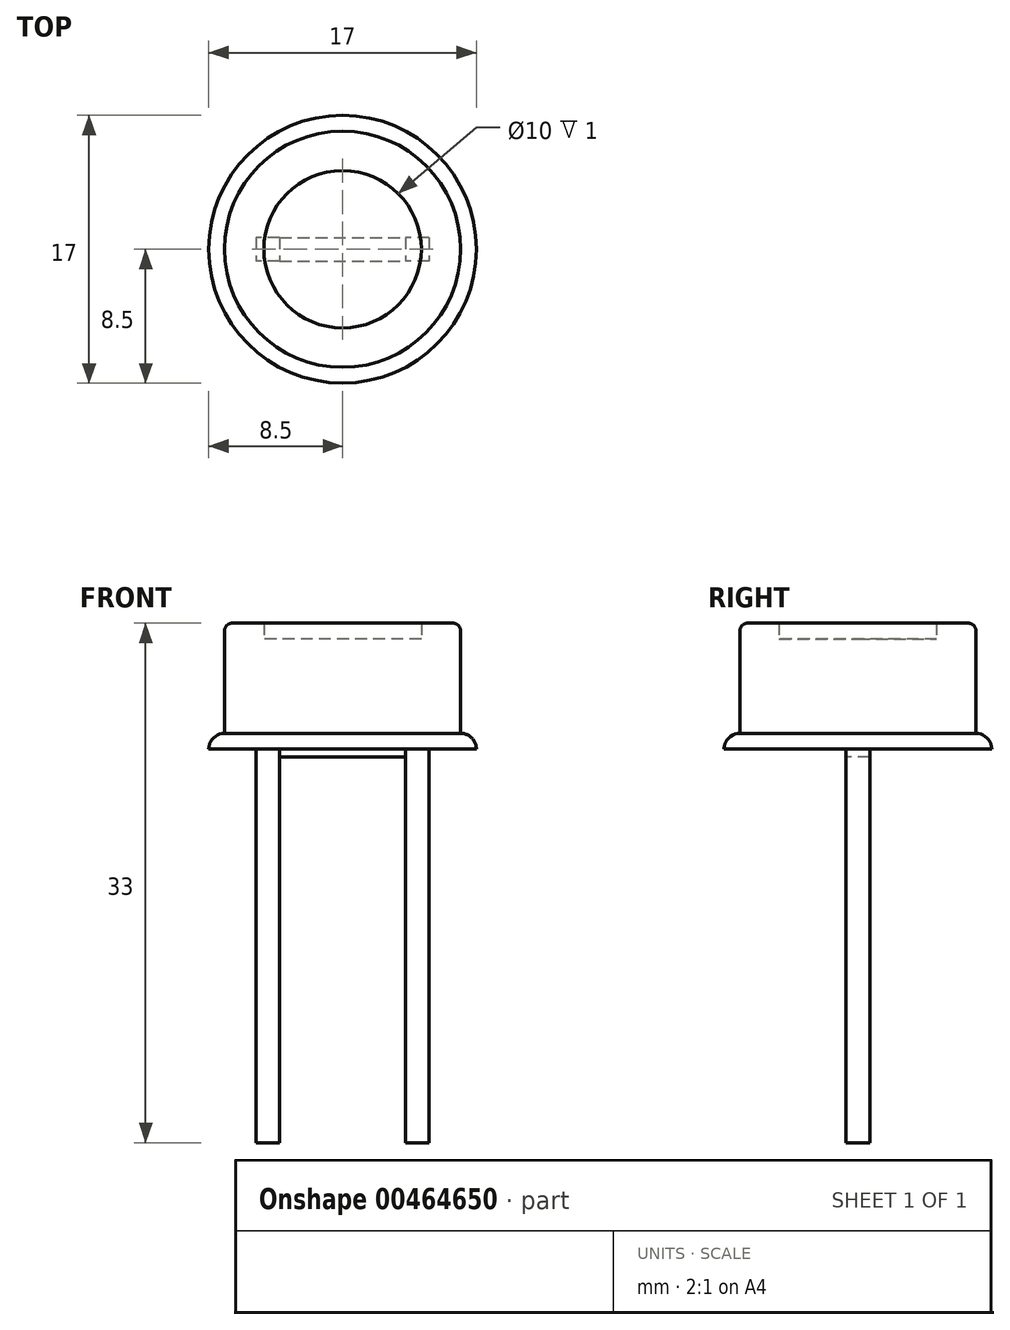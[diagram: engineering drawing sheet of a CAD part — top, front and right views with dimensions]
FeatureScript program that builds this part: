
annotation { "Feature Type Name" : "Feature", "Feature Type Description" : "" }
export const myFeature = defineFeature(function(context is Context, id is Id, definition is map)
    precondition{}
    {
        {
            var Q0;
            Q0=qCreatedBy(makeId("Top.planeOp"),FACE);
            var sketch = newSketch(context, id + "F0", { "sketchPlane" : qUnion([Q0])});
            skCircle(sketch, "E0", {"center": v(0, 0) * mm, "radius": 7.5 * mm});
            skCircle(sketch, "E1", {"center": v(0, 0) * mm, "radius": 5 * mm});
            skCircle(sketch, "E2", {"center": v(0, 0) * mm, "radius": 8.5 * mm});
            skSolve(sketch);
        }
        {
            var Q0;
            Q0=makeQuery(id+"F0.imprint","IMPRINT",FACE,{"disambiguationData":[TD([[makeQuery(id+"F0.imprint","IMPRINT",EDGE,{"derivedFrom":sQuery(id+"F0.wireOp",EDGE,"E1")}),1.0]])]});
            extrude(context, id + "F1", {"entities" : qUnion([Q0]), "depth" : 7 * mm});
        }
        {
            var Q0;
            Q0=makeQuery(id+"F0.imprint","IMPRINT",FACE,{"disambiguationData":[TD([[makeQuery(id+"F0.imprint","IMPRINT",EDGE,{"derivedFrom":sQuery(id+"F0.wireOp",EDGE,"E0")}),1.0]])]});
            extrude(context, id + "F2", {"entities" : qUnion([Q0]), "operationType" : NewBodyOperationType.ADD, "depth" : 8 * mm});
        }
        {
            var Q0;
            Q0=makeQuery(id+"F0.imprint","IMPRINT",FACE,{"disambiguationData":[TD([[makeQuery(id+"F0.imprint","IMPRINT",EDGE,{"derivedFrom":sQuery(id+"F0.wireOp",EDGE,"E0")}),-1.0]])]});
            extrude(context, id + "F3", {"entities" : qUnion([Q0]), "operationType" : NewBodyOperationType.ADD, "depth" : 1 * mm});
        }
        {
            var Q0;
            Q0=makeQuery(id+"F3.opExtrude","CAP_EDGE",EDGE,{"disambiguationData":[OSD([sQuery(id+"F0.wireOp",EDGE,"E2")])],"isStart":false});
            fillet(context, id + "F4", {"entities" : qUnion([Q0]), "radius" : 1 * mm, "tangentPropagation" : true, "allowEdgeOverflow" : false});
        }
        {
            var Q0;
            Q0=makeQuery(id+"F2.opExtrude","CAP_EDGE",EDGE,{"disambiguationData":[OSD([sQuery(id+"F0.wireOp",EDGE,"E0")])],"isStart":false});
            fillet(context, id + "F5", {"entities" : qUnion([Q0]), "radius" : .5 * mm, "tangentPropagation" : true, "allowEdgeOverflow" : false});
        }
        {
            var Q0;
            {var subQ0=sQuery(id+"F0.wireOp",EDGE,"E0");var subQ1=sQuery(id+"F0.wireOp",EDGE,"E1");Q0=makeQuery(id+"F3.boolean.opBoolean","MERGE",FACE,{"derivedFrom":[makeQuery(id+"F2.boolean.opBoolean","MERGE",FACE,{"derivedFrom":[makeQuery(id+"F1.opExtrude","CAP_FACE",FACE,{"disambiguationData":[OSD([subQ1])],"isStart":true}),makeQuery(id+"F2.opExtrude","CAP_FACE",FACE,{"disambiguationData":[OSD([subQ0,subQ1])],"isStart":true})]}),makeQuery(id+"F3.opExtrude","CAP_FACE",FACE,{"disambiguationData":[OSD([subQ0,sQuery(id+"F0.wireOp",EDGE,"E2")])],"isStart":true})]});}
            var sketch = newSketch(context, id + "F6", { "sketchPlane" : qUnion([Q0])});
            skLineSegment(sketch, "E3.bottom", {"start": v(5.5, -0.75) * mm, "end": v(4, -0.75) * mm});
            skLineSegment(sketch, "E3.top", {"start": v(5.5, 0.75) * mm, "end": v(4, 0.75) * mm});
            skLineSegment(sketch, "E3.left", {"start": v(5.5, -0.75) * mm, "end": v(5.5, 0.75) * mm});
            skLineSegment(sketch, "E3.right", {"start": v(4, -0.75) * mm, "end": v(4, 0.75) * mm});
            skPoint(sketch, "E3.middle", {"position": v(4.75, 0) * mm});
            skLineSegment(sketch, "E4.bottom", {"start": v(-4, -0.75) * mm, "end": v(-5.5, -0.75) * mm});
            skLineSegment(sketch, "E4.top", {"start": v(-4, 0.75) * mm, "end": v(-5.5, 0.75) * mm});
            skLineSegment(sketch, "E4.left", {"start": v(-4, -0.75) * mm, "end": v(-4, 0.75) * mm});
            skLineSegment(sketch, "E4.right", {"start": v(-5.5, -0.75) * mm, "end": v(-5.5, 0.75) * mm});
            skPoint(sketch, "E4.middle", {"position": v(-4.75, 0) * mm});
            skLineSegment(sketch, "E5.bottom", {"start": v(-4, 0.75) * mm, "end": v(4, 0.75) * mm});
            skLineSegment(sketch, "E5.top", {"start": v(-4, -0.75) * mm, "end": v(4, -0.75) * mm});
            skLineSegment(sketch, "E5.left", {"start": v(-4, 0.75) * mm, "end": v(-4, -0.75) * mm});
            skLineSegment(sketch, "E5.right", {"start": v(4, 0.75) * mm, "end": v(4, -0.75) * mm});
            skSolve(sketch);
        }
        {
            var Q0;
            Q0=makeQuery(id+"F6.imprint","IMPRINT",FACE,{"disambiguationData":[TD([[makeQuery(id+"F6.imprint","IMPRINT",EDGE,{"derivedFrom":sQuery(id+"F6.wireOp",EDGE,"E4.bottom")}),-1.0]])]});
            var Q1;
            Q1=makeQuery(id+"F6.imprint","IMPRINT",FACE,{"disambiguationData":[TD([[makeQuery(id+"F6.imprint","IMPRINT",EDGE,{"derivedFrom":sQuery(id+"F6.wireOp",EDGE,"E3.bottom")}),-1.0]])]});
            extrude(context, id + "F7", {"entities" : qUnion([Q0, Q1]), "depth" : 25 * mm});
        }
        {
            var Q0;
            Q0=makeQuery(id+"F6.imprint","IMPRINT",FACE,{"disambiguationData":[TD([[makeQuery(id+"F6.imprint","IMPRINT",EDGE,{"derivedFrom":sQuery(id+"F6.wireOp",EDGE,"E5.bottom")}),-1.0]])]});
            var sketch = newSketch(context, id + "F8", { "sketchPlane" : qUnion([Q0])});
            skSolve(sketch);
        }
        {
            var Q0;
            Q0 = qSketchRegion(id + "F8", true);
            var Q1;
            Q1=makeQuery(id+"F6.imprint","IMPRINT",FACE,{"disambiguationData":[TD([[makeQuery(id+"F6.imprint","IMPRINT",EDGE,{"derivedFrom":sQuery(id+"F6.wireOp",EDGE,"E5.bottom")}),-1.0]])]});
            extrude(context, id + "F9", {"entities" : qUnion([Q0, Q1]), "depth" : .5 * mm});
        }
    });
